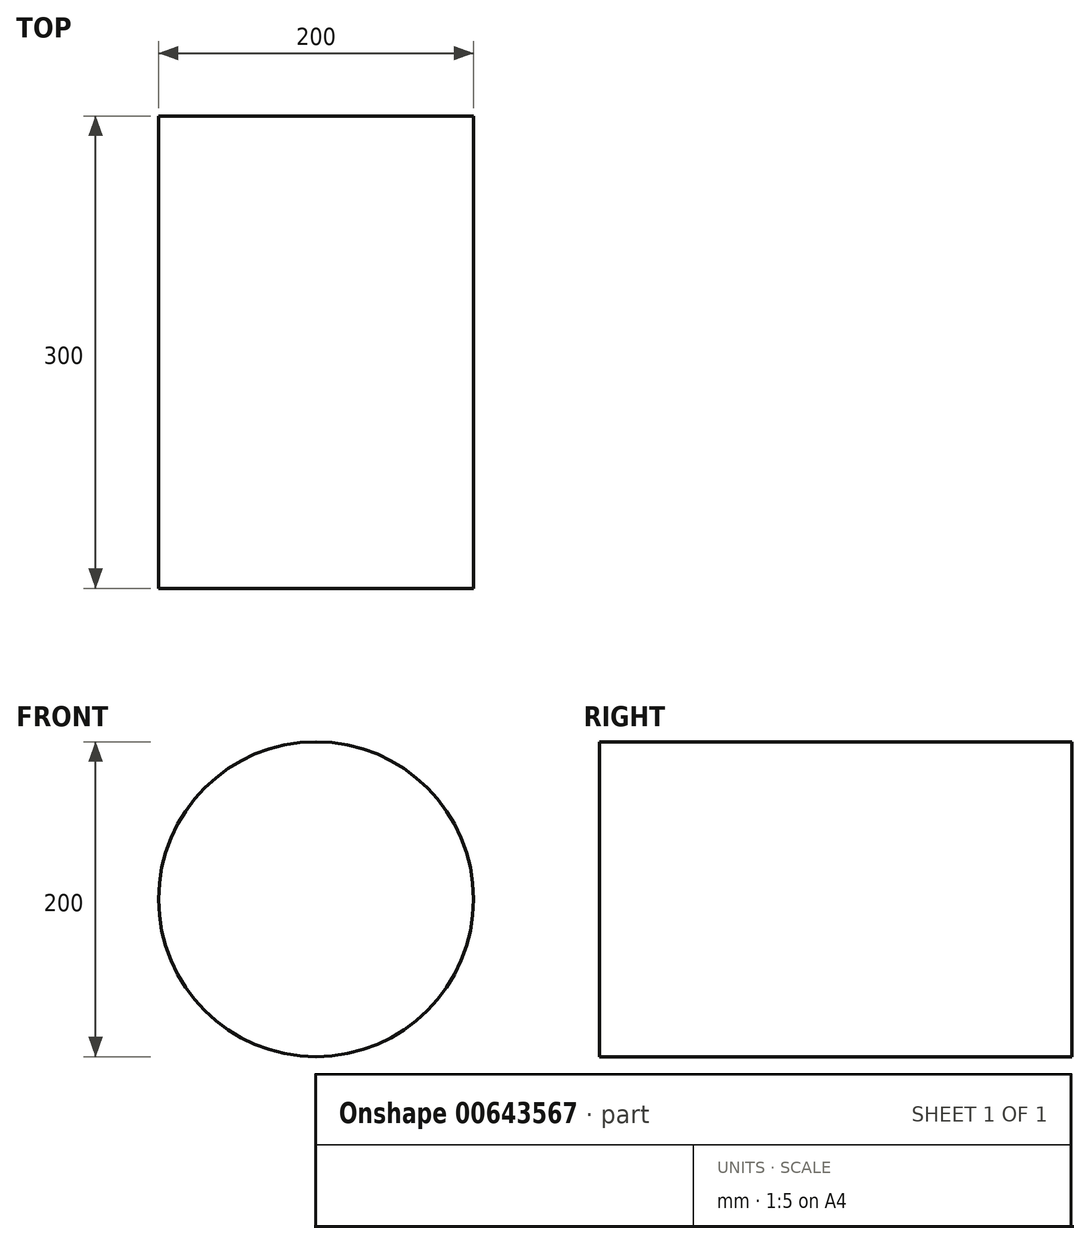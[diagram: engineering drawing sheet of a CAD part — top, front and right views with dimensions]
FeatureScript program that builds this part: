
annotation { "Feature Type Name" : "Feature", "Feature Type Description" : "" }
export const myFeature = defineFeature(function(context is Context, id is Id, definition is map)
    precondition{}
    {
        {
            var Q0;
            Q0=qCreatedBy(makeId("Front.planeOp"),FACE);
            var sketch = newSketch(context, id + "F0", { "sketchPlane" : qUnion([Q0])});
            skCircle(sketch, "E0", {"center": v(0, 0) * mm, "radius": 100 * mm});
            skSolve(sketch);
        }
        {
            var Q0;
            Q0 = qSketchRegion(id + "F0", true);
            extrude(context, id + "F1", {"entities" : qUnion([Q0]), "depth" : 150 * mm, "offsetDistance" : 25 * mm, "hasSecondDirection" : true, "secondDirectionOppositeDirection" : true, "secondDirectionDepth" : 150 * mm});
        }
    });
